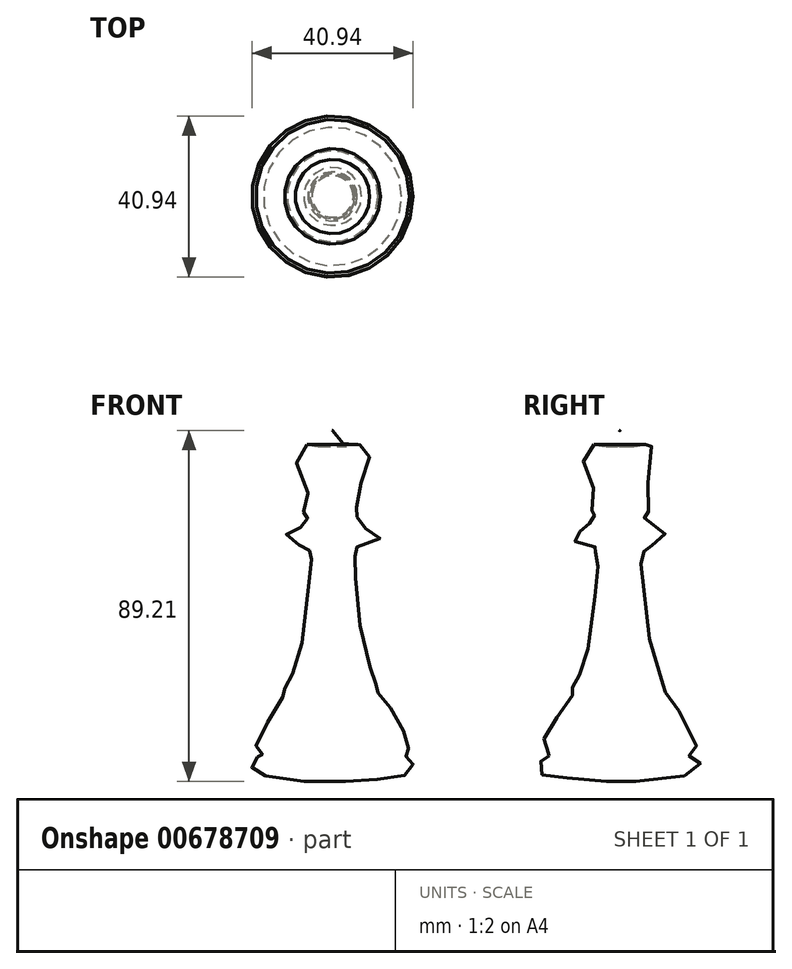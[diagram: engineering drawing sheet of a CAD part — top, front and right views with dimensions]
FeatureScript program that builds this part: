
annotation { "Feature Type Name" : "Feature", "Feature Type Description" : "" }
export const myFeature = defineFeature(function(context is Context, id is Id, definition is map)
    precondition{}
    {
        {
            var Q0;
            Q0=qCreatedBy(makeId("Front.planeOp"),FACE);
            var sketch = newSketch(context, id + "F0", { "sketchPlane" : qUnion([Q0])});
            skFitSpline(sketch, "E0", {"points": [v(0, -43.79) * mm, v(9.8, -43.48) * mm, v(17.48, -42.32) * mm, v(20.2, -41.64) * mm, v(20.46, -39.28) * mm, v(20.45, -39.22) * mm, v(19.48, -38) * mm, v(18.5, -37.34) * mm, v(17.58, -37.2) * mm, v(19.17, -35.5) * mm, v(19.12, -32.64) * mm, v(16.63, -28.98) * mm, v(13.26, -23) * mm, v(11.53, -21.3) * mm, v(12.15, -20.33) * mm, v(11.36, -19.35) * mm, v(10.98, -19.1) * mm, v(10.6, -17.9) * mm, v(7.65, -8.1) * mm, v(5.58, 10.36) * mm, v(5.5, 13.23) * mm, v(6.25, 14.32) * mm, v(5.65, 15.46) * mm, v(10.34, 16.72) * mm, v(12.05, 18.73) * mm, v(8.46, 20.42) * mm, v(7.5, 22) * mm, v(6.23, 23.45) * mm, v(7.34, 24.6) * mm, v(6.22, 25.7) * mm, v(6.5, 30.26) * mm, v(9.25, 37.59) * mm, v(9.1, 40.4) * mm, v(6.64, 41.78) * mm, v(2.96, 41.51) * mm, v(2.58, 43.6) * mm, v(0, 45.39) * mm], "startDerivative": vector(221.52, -3.01) * mm, "endDerivative": vector(-170.45, -3.81) * mm});
            skLineSegment(sketch, "E1", {"start": v(0, 50.9) * mm, "end": v(0, -52.62) * mm, "construction": true});
            skSolve(sketch);
        }
        {
            var Q0;
            Q0=sQuery(id+"F0.wireOp",EDGE,"E0");
            var Q1;
            Q1=sQuery(id+"F0.wireOp",EDGE,"E1");
            revolve(context, id + "F1", {"bodyType" : ToolBodyType.SURFACE, "surfaceEntities" : qUnion([Q0]), "axis" : qUnion([Q1]), "revolveType" : RevolveType.FULL});
        }
    });
